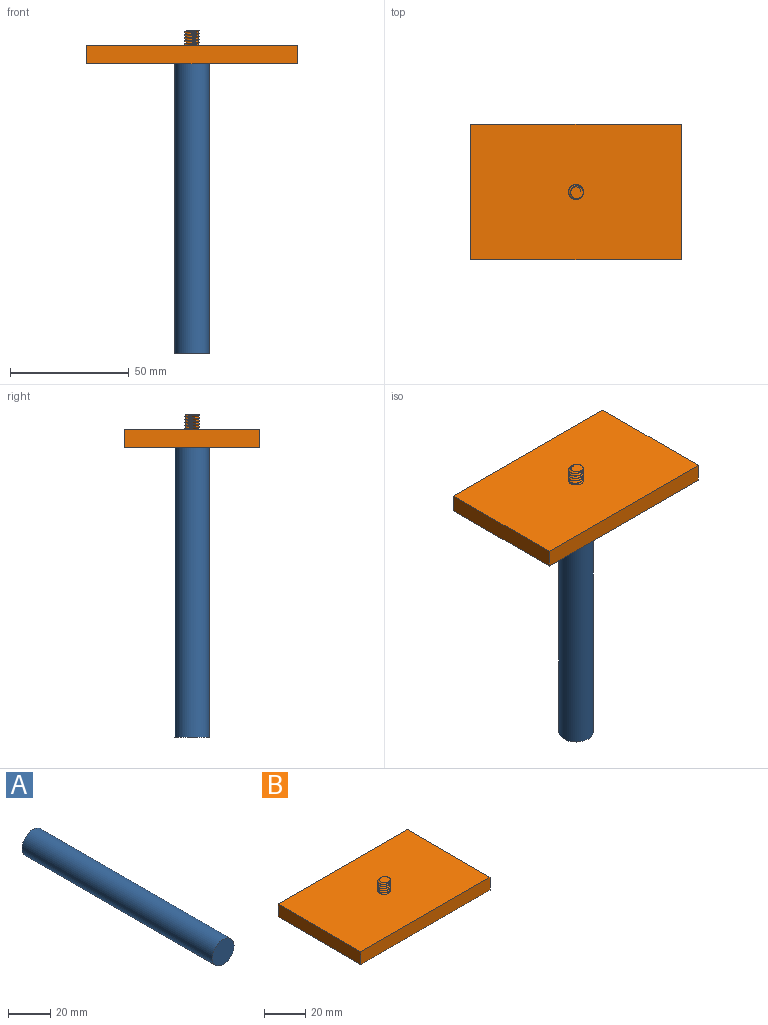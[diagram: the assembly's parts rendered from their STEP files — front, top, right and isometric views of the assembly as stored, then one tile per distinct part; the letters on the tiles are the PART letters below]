
ASSEMBLY  parts=2 mates=1
PART A: 3 faces, bbox 14.5x127x14.5 mm
  f0: cylinder r=7.24mm len=127mm, axis (0,1,0), area 5776.5mm2, adj f1,f2
  f1: plane 14.48x14.48mm, normal (0,-1,0), area 164.6mm2, adj f0
  f2: plane 14.48x14.48mm, normal (0,1,0), area 164.6mm2, adj f0
PART B: 14 faces, bbox 89.6x57.9x15.4 mm
  f0: cylinder r=3.11mm len=6.35mm, axis (0,0,-1), area 11.6mm2, adj f5,f7,f10,f11
  f1: plane 88.9x7.62mm, normal (0,-1,0), area 677.4mm2, adj f2,f4,f5,f6
  f2: plane 57.15x7.62mm, normal (1,0,0), area 435.5mm2, adj f1,f3,f5,f6
  f3: plane 88.9x7.62mm, normal (0,1,0), area 677.4mm2, adj f2,f4,f5,f6
  f4: plane 57.15x7.62mm, normal (-1,0,0), area 435.5mm2, adj f1,f3,f5,f6
  f5: plane 88.9x57.15mm, normal (0,0,1), area 5050.2mm2, adj f0,f1,f2,f3,f4,f9
  f6: plane 88.9x57.15mm, normal (0,0,-1), area 4910.2mm2, adj f1,f2,f3,f4,f13
  f7: plane 6.12x6.1mm, normal (0,0,1), area 22.6mm2, adj f0,f10,f11
  f8: plane 1.14x0.99mm, normal (0,1,0), area 0.6mm2, adj f9,f10,f11
  f9: cylinder r=3.11mm len=6.22mm, axis (0,0,1), area 10.1mm2, adj f5,f8,f10
  f10: bspline ~8.19x7.19mm, area 107.1mm2, adj f0,f7,f8,f9,f11
  f11: bspline ~7.56x7.19mm, area 98mm2, adj f0,f7,f8,f10
  f12: cone r=0mm half-angle=59deg, axis (0,0,-1), area 198.9mm2, adj f13
  f13: cylinder r=7.37mm len=14.73mm, axis (0,0,-1), area 117.6mm2, adj f6,f12
PLACE A rot(axis=(-1,0,0),90deg) t=(-29.38,25.4,-106.47)mm
PLACE B t=(-29.38,25.4,15.78)mm
MATE fastened A.f0 <-> B.f12  axis (0,0,1) through (-29.38,25.4,20.53)mm
